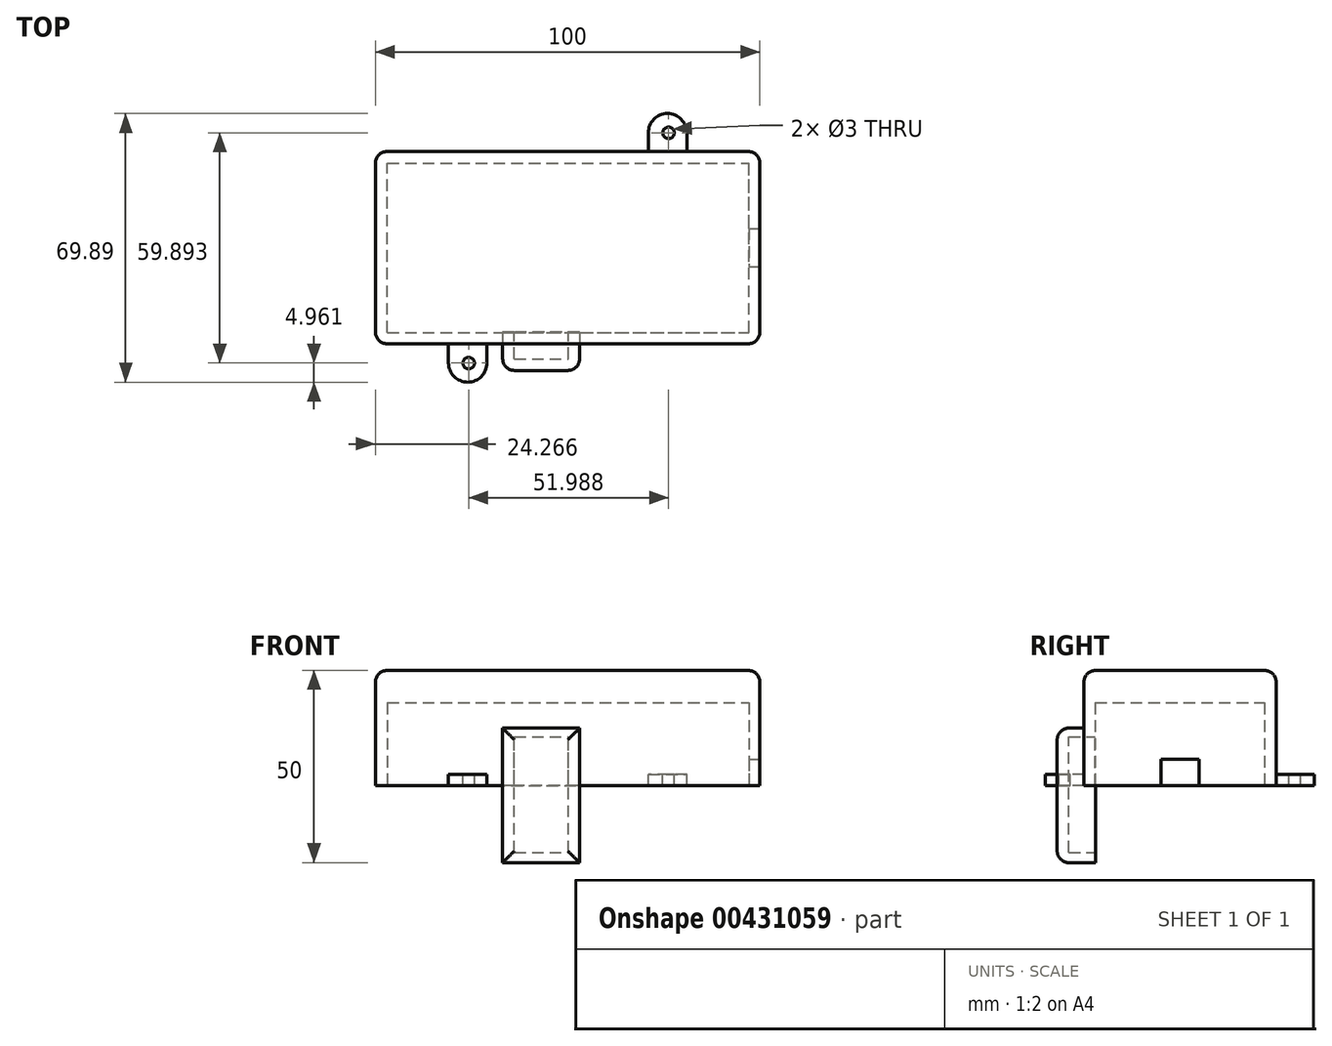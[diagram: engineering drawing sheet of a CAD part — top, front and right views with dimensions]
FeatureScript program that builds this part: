
annotation { "Feature Type Name" : "Feature", "Feature Type Description" : "" }
export const myFeature = defineFeature(function(context is Context, id is Id, definition is map)
    precondition{}
    {
        {
            var Q0;
            Q0=qCreatedBy(makeId("Top.planeOp"),FACE);
            var sketch = newSketch(context, id + "F0", { "sketchPlane" : qUnion([Q0])});
            skLineSegment(sketch, "E0.bottom", {"start": v(60.88, 30.02) * mm, "end": v(-39.12, 30.02) * mm});
            skLineSegment(sketch, "E0.top", {"start": v(60.88, -19.98) * mm, "end": v(-39.12, -19.98) * mm});
            skLineSegment(sketch, "E0.left", {"start": v(60.88, 30.02) * mm, "end": v(60.88, -19.98) * mm});
            skLineSegment(sketch, "E0.right", {"start": v(-39.12, 30.02) * mm, "end": v(-39.12, -19.98) * mm});
            skSolve(sketch);
        }
        {
            var Q0;
            Q0=qCreatedBy(makeId("Top.planeOp"),FACE);
            var sketch = newSketch(context, id + "F1", { "sketchPlane" : qUnion([Q0])});
            skLineSegment(sketch, "E1.left", {"start": v(31.87, 24.9) * mm, "end": v(31.87, 34.9) * mm});
            skLineSegment(sketch, "E2.MirrorCS", {"start": v(31.87, 24.9) * mm, "end": v(41.87, 24.9) * mm});
            skCircle(sketch, "E3.MirrorC", {"center": v(36.87, 34.9) * mm, "radius": 5 * mm});
            skLineSegment(sketch, "E4.MirrorCS", {"start": v(31.87, 34.9) * mm, "end": v(41.87, 34.9) * mm});
            skLineSegment(sketch, "E5.MirrorCS", {"start": v(60.87, 24.9) * mm, "end": v(31.87, 24.9) * mm, "construction": true});
            skLineSegment(sketch, "E6.MirrorCS", {"start": v(41.87, 24.9) * mm, "end": v(41.87, 34.9) * mm});
            skLineSegment(sketch, "E7", {"start": v(60.87, 24.9) * mm, "end": v(60.87, 29.9) * mm, "construction": true});
            skLineSegment(sketch, "E8", {"start": v(-39.15, -14.79) * mm, "end": v(-39.15, -19.79) * mm, "construction": true});
            skLineSegment(sketch, "E9.left", {"start": v(-10.1, -14.99) * mm, "end": v(-10.1, -24.99) * mm});
            skLineSegment(sketch, "E10.MirrorCS", {"start": v(-10.1, -14.99) * mm, "end": v(-20.1, -14.99) * mm});
            skCircle(sketch, "E11.MirrorC", {"center": v(-15.1, -24.99) * mm, "radius": 5 * mm});
            skLineSegment(sketch, "E12.MirrorCS", {"start": v(-10.1, -24.99) * mm, "end": v(-20.1, -24.99) * mm});
            skLineSegment(sketch, "E13.MirrorCS", {"start": v(-39.1, -14.99) * mm, "end": v(-10.1, -14.99) * mm, "construction": true});
            skLineSegment(sketch, "E14.MirrorCS", {"start": v(-20.1, -14.99) * mm, "end": v(-20.1, -24.99) * mm});
            skLineSegment(sketch, "E15", {"start": v(-39.1, -14.99) * mm, "end": v(-39.1, -19.99) * mm, "construction": true});
            skSolve(sketch);
        }
        {
            var Q0;
            {var subQ0=sQuery(id+"F1.wireOp",EDGE,"E1.left");Q0=makeQuery(id+"F1.imprint","IMPRINT",FACE,{"disambiguationData":[TD([[makeQuery(id+"F1.imprint","IMPRINT",EDGE,{"derivedFrom":subQ0}),-1.0]])]});}
            var Q1;
            {var subQ0=sQuery(id+"F1.wireOp",EDGE,"E4.MirrorCS");Q1=makeQuery(id+"F1.imprint","IMPRINT",FACE,{"disambiguationData":[TD([[makeQuery(id+"F1.imprint","IMPRINT",EDGE,{"derivedFrom":subQ0}),-1.0]])]});}
            var Q2;
            {var subQ0=sQuery(id+"F1.wireOp",EDGE,"E4.MirrorCS");Q2=makeQuery(id+"F1.imprint","IMPRINT",FACE,{"disambiguationData":[TD([[makeQuery(id+"F1.imprint","IMPRINT",EDGE,{"derivedFrom":subQ0}),1.0]])]});}
            var Q3;
            {var subQ0=sQuery(id+"F1.wireOp",EDGE,"7076a85a-518e-4b84-a5a1-eae27ff6416b.MirrorCS");Q3=makeQuery(id+"F1.imprint","IMPRINT",FACE,{"disambiguationData":[TD([[makeQuery(id+"F1.imprint","IMPRINT",EDGE,{"derivedFrom":subQ0}),1.0]])]});}
            var Q4;
            {var subQ0=sQuery(id+"F1.wireOp",EDGE,"7076a85a-518e-4b84-a5a1-eae27ff6416b.MirrorCS");Q4=makeQuery(id+"F1.imprint","IMPRINT",FACE,{"disambiguationData":[TD([[makeQuery(id+"F1.imprint","IMPRINT",EDGE,{"derivedFrom":subQ0}),-1.0]])]});}
            var Q5;
            {var subQ0=sQuery(id+"F1.wireOp",EDGE,"5b771f0d-63e5-45e8-b39b-5c0f41a443e1.left");Q5=makeQuery(id+"F1.imprint","IMPRINT",FACE,{"disambiguationData":[TD([[makeQuery(id+"F1.imprint","IMPRINT",EDGE,{"derivedFrom":subQ0}),-1.0]])]});}
            var Q6;
            {var subQ0=sQuery(id+"F1.wireOp",EDGE,"E12.MirrorCS");Q6=makeQuery(id+"F1.imprint","IMPRINT",FACE,{"disambiguationData":[TD([[makeQuery(id+"F1.imprint","IMPRINT",EDGE,{"derivedFrom":subQ0}),1.0]])]});}
            var Q7;
            {var subQ0=sQuery(id+"F1.wireOp",EDGE,"E12.MirrorCS");Q7=makeQuery(id+"F1.imprint","IMPRINT",FACE,{"disambiguationData":[TD([[makeQuery(id+"F1.imprint","IMPRINT",EDGE,{"derivedFrom":subQ0}),-1.0]])]});}
            var Q8;
            {var subQ0=sQuery(id+"F1.wireOp",EDGE,"E9.left");Q8=makeQuery(id+"F1.imprint","IMPRINT",FACE,{"disambiguationData":[TD([[makeQuery(id+"F1.imprint","IMPRINT",EDGE,{"derivedFrom":subQ0}),-1.0]])]});}
            extrude(context, id + "F2", {"entities" : qUnion([Q0, Q1, Q2, Q3, Q4, Q5, Q6, Q7, Q8]), "depth" : 3 * mm});
        }
        {
            var Q0;
            Q0=makeQuery(id+"F0.imprint","IMPRINT",FACE,{"disambiguationData":[TD([[makeQuery(id+"F0.imprint","IMPRINT",EDGE,{"derivedFrom":sQuery(id+"F0.wireOp",EDGE,"E0.bottom")}),1.0]])]});
            extrude(context, id + "F3", {"entities" : qUnion([Q0]), "operationType" : NewBodyOperationType.ADD, "depth" : 30 * mm});
        }
        {
            var Q0;
            Q0=makeQuery(id+"F3.opExtrude","CAP_EDGE",EDGE,{"disambiguationData":[OSD([sQuery(id+"F0.wireOp",EDGE,"E0.bottom")])],"isStart":false});
            var Q1;
            Q1=makeQuery(id+"F3.opExtrude","CAP_EDGE",EDGE,{"disambiguationData":[OSD([sQuery(id+"F0.wireOp",EDGE,"E0.left")])],"isStart":false});
            var Q2;
            Q2=makeQuery(id+"F3.opExtrude","CAP_EDGE",EDGE,{"disambiguationData":[OSD([sQuery(id+"F0.wireOp",EDGE,"E0.top")])],"isStart":false});
            var Q3;
            Q3=makeQuery(id+"F3.opExtrude","CAP_EDGE",EDGE,{"disambiguationData":[OSD([sQuery(id+"F0.wireOp",EDGE,"E0.right")])],"isStart":false});
            var Q4;
            Q4=makeQuery(id+"F3.opExtrude","SWEPT_EDGE",EDGE,{"disambiguationData":[OSD([sQuery(id+"F0.wireOp",EDGE,"E0.bottom"),sQuery(id+"F0.wireOp",EDGE,"E0.left")])]});
            var Q5;
            Q5=makeQuery(id+"F3.opExtrude","SWEPT_EDGE",EDGE,{"disambiguationData":[OSD([sQuery(id+"F0.wireOp",EDGE,"E0.bottom"),sQuery(id+"F0.wireOp",EDGE,"E0.right")])]});
            var Q6;
            Q6=makeQuery(id+"F3.opExtrude","SWEPT_EDGE",EDGE,{"disambiguationData":[OSD([sQuery(id+"F0.wireOp",EDGE,"E0.top"),sQuery(id+"F0.wireOp",EDGE,"E0.left")])]});
            var Q7;
            Q7=makeQuery(id+"F3.opExtrude","SWEPT_EDGE",EDGE,{"disambiguationData":[OSD([sQuery(id+"F0.wireOp",EDGE,"E0.top"),sQuery(id+"F0.wireOp",EDGE,"E0.right")])]});
            fillet(context, id + "F4", {"entities" : qUnion([Q0, Q1, Q2, Q3, Q4, Q5, Q6, Q7]), "radius" : 3 * mm, "tangentPropagation" : true, "allowEdgeOverflow" : false});
        }
        {
            var Q0;
            Q0=makeQuery(id+"F0.imprint","IMPRINT",FACE,{"disambiguationData":[TD([[makeQuery(id+"F0.imprint","IMPRINT",EDGE,{"derivedFrom":sQuery(id+"F0.wireOp",EDGE,"E0.bottom")}),1.0]])]});
            var sketch = newSketch(context, id + "F5", { "sketchPlane" : qUnion([Q0])});
            skLineSegment(sketch, "E16.bottom", {"start": v(-36, -17.05) * mm, "end": v(58, -17.05) * mm});
            skLineSegment(sketch, "E16.top", {"start": v(-36, 26.95) * mm, "end": v(58, 26.95) * mm});
            skLineSegment(sketch, "E16.left", {"start": v(-36, -17.05) * mm, "end": v(-36, 26.95) * mm});
            skLineSegment(sketch, "E16.right", {"start": v(58, -17.05) * mm, "end": v(58, 26.95) * mm});
            skSolve(sketch);
        }
        {
            var Q0;
            Q0=makeQuery(id+"F2.opExtrude","CAP_FACE",FACE,{"disambiguationData":[OSD([sQuery(id+"F1.wireOp",EDGE,"E1.bottom"),sQuery(id+"F1.wireOp",EDGE,"E1.left"),sQuery(id+"F1.wireOp",EDGE,"E1.right"),sQuery(id+"F1.wireOp",EDGE,"xwiUSXtl-78BE-kdJO-Y9RC-46X8hIM0eXsI")])],"isStart":false});
            var sketch = newSketch(context, id + "F6", { "sketchPlane" : qUnion([Q0])});
            skCircle(sketch, "E17", {"center": v(37.13, 34.86) * mm, "radius": 1.5 * mm});
            skCircle(sketch, "E18", {"center": v(-14.85, -25.03) * mm, "radius": 1.5 * mm});
            skSolve(sketch);
        }
        {
            var Q0;
            Q0 = qSketchRegion(id + "F6", true);
            extrude(context, id + "F7", {"entities" : qUnion([Q0]), "operationType" : NewBodyOperationType.REMOVE, "oppositeDirection" : true, "depth" : 10 * mm});
        }
        {
            var Q0;
            Q0=qCreatedBy(makeId("Top.planeOp"),FACE);
            var sketch = newSketch(context, id + "F8", { "sketchPlane" : qUnion([Q0])});
            skLineSegment(sketch, "E19", {"start": v(-39.01, -16.94) * mm, "end": v(13.99, -16.94) * mm, "construction": true});
            skLineSegment(sketch, "E20.bottom", {"start": v(13.99, -16.94) * mm, "end": v(-6.01, -16.94) * mm});
            skLineSegment(sketch, "E20.top", {"start": v(13.99, -26.94) * mm, "end": v(-6.01, -26.94) * mm});
            skLineSegment(sketch, "E20.left", {"start": v(13.99, -16.94) * mm, "end": v(13.99, -26.94) * mm});
            skLineSegment(sketch, "E20.right", {"start": v(-6.01, -16.94) * mm, "end": v(-6.01, -26.94) * mm});
            skSolve(sketch);
        }
        {
            var Q0;
            Q0=makeQuery(id+"F8.imprint","IMPRINT",FACE,{"disambiguationData":[TD([[makeQuery(id+"F8.imprint","IMPRINT",EDGE,{"derivedFrom":sQuery(id+"F8.wireOp",EDGE,"E20.bottom")}),1.0]])]});
            extrude(context, id + "F9", {"entities" : qUnion([Q0]), "oppositeDirection" : true, "depth" : 20 * mm});
        }
        {
            var Q0;
            Q0=makeQuery(id+"F8.imprint","IMPRINT",FACE,{"disambiguationData":[TD([[makeQuery(id+"F8.imprint","IMPRINT",EDGE,{"derivedFrom":sQuery(id+"F8.wireOp",EDGE,"E20.bottom")}),1.0]])]});
            extrude(context, id + "F10", {"entities" : qUnion([Q0]), "operationType" : NewBodyOperationType.ADD, "depth" : 15 * mm});
        }
        {
            var Q0;
            {var subQ0=sQuery(id+"F8.wireOp",EDGE,"E20.bottom");Q0=makeQuery(id+"F10.boolean.opBoolean","MERGE",FACE,{"derivedFrom":[makeQuery(id+"F9.opExtrude","SWEPT_FACE",FACE,{"disambiguationData":[OSD([subQ0])]}),makeQuery(id+"F10.opExtrude","SWEPT_FACE",FACE,{"disambiguationData":[OSD([subQ0])]})]});}
            var sketch = newSketch(context, id + "F11", { "sketchPlane" : qUnion([Q0])});
            skLineSegment(sketch, "E21.bottom", {"start": v(2.98, -17.3) * mm, "end": v(-11.02, -17.3) * mm});
            skLineSegment(sketch, "E21.top", {"start": v(2.98, 12.7) * mm, "end": v(-11.02, 12.7) * mm});
            skLineSegment(sketch, "E21.left", {"start": v(2.98, -17.3) * mm, "end": v(2.98, 12.7) * mm});
            skLineSegment(sketch, "E21.right", {"start": v(-11.02, -17.3) * mm, "end": v(-11.02, 12.7) * mm});
            skSolve(sketch);
        }
        {
            var Q0;
            Q0 = qSketchRegion(id + "F5", true);
            var Q1;
            Q1=sQuery(id+"F5.wireOp",EDGE,"E16.left");
            var Q2;
            Q2=sQuery(id+"F5.wireOp",EDGE,"E16.bottom");
            var Q3;
            Q3=sQuery(id+"F5.wireOp",EDGE,"E16.right");
            var Q4;
            Q4=sQuery(id+"F5.wireOp",EDGE,"E16.top");
            extrude(context, id + "F12", {"entities" : qUnion([Q0]), "operationType" : NewBodyOperationType.REMOVE, "surfaceEntities" : qUnion([Q1, Q2, Q3, Q4]), "depth" : 21.6 * mm});
        }
        {
            var Q0;
            {var subQ0=sQuery(id+"F11.wireOp",EDGE,"E21.top");Q0=makeQuery(id+"F11.imprint","IMPRINT",FACE,{"disambiguationData":[TD([[makeQuery(id+"F11.imprint","IMPRINT",EDGE,{"derivedFrom":subQ0}),1.0]])]});}
            var Q1;
            {var subQ0=sQuery(id+"F11.wireOp",EDGE,"E21.bottom");Q1=makeQuery(id+"F11.imprint","IMPRINT",FACE,{"disambiguationData":[TD([[makeQuery(id+"F11.imprint","IMPRINT",EDGE,{"derivedFrom":subQ0}),-1.0]])]});}
            extrude(context, id + "F13", {"entities" : qUnion([Q0, Q1]), "operationType" : NewBodyOperationType.REMOVE, "oppositeDirection" : true, "depth" : 7 * mm});
        }
        {
            var Q0;
            {var subQ0=sQuery(id+"F8.wireOp",EDGE,"E20.top");Q0=makeQuery(id+"F10.boolean.opBoolean","MERGE",FACE,{"derivedFrom":[makeQuery(id+"F9.opExtrude","SWEPT_FACE",FACE,{"disambiguationData":[OSD([subQ0])]}),makeQuery(id+"F10.opExtrude","SWEPT_FACE",FACE,{"disambiguationData":[OSD([subQ0])]})]});}
            fillet(context, id + "F14", {"entities" : qUnion([Q0]), "radius" : 3 * mm, "tangentPropagation" : true, "allowEdgeOverflow" : false});
        }
        {
            var Q0;
            Q0=makeQuery(id+"F3.opExtrude","SWEPT_FACE",FACE,{"disambiguationData":[OSD([sQuery(id+"F0.wireOp",EDGE,"E0.left")])]});
            var sketch = newSketch(context, id + "F15", { "sketchPlane" : qUnion([Q0])});
            skLineSegment(sketch, "E22", {"start": v(-20, 0) * mm, "end": v(5, 0) * mm, "construction": true});
            skLineSegment(sketch, "E23", {"start": v(5, 0) * mm, "end": v(0, 0) * mm, "construction": true});
            skLineSegment(sketch, "E24.bottom", {"start": v(0, 0) * mm, "end": v(0, 6.9) * mm});
            skLineSegment(sketch, "E24.top", {"start": v(10, 0) * mm, "end": v(10, 6.9) * mm});
            skLineSegment(sketch, "E24.left", {"start": v(0, 0) * mm, "end": v(10, 0) * mm});
            skLineSegment(sketch, "E24.right", {"start": v(0, 6.9) * mm, "end": v(10, 6.9) * mm});
            skSolve(sketch);
        }
        {
            var Q0;
            Q0=makeQuery(id+"F15.imprint","IMPRINT",FACE,{"disambiguationData":[TD([[makeQuery(id+"F15.imprint","IMPRINT",EDGE,{"derivedFrom":sQuery(id+"F15.wireOp",EDGE,"E24.bottom")}),-1.0]])]});
            extrude(context, id + "F16", {"entities" : qUnion([Q0]), "operationType" : NewBodyOperationType.REMOVE, "oppositeDirection" : true, "depth" : 10 * mm});
        }
    });
